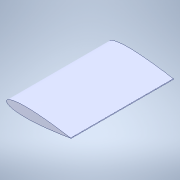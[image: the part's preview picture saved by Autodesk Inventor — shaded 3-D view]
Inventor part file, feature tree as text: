
AUTODESK INVENTOR PART (.ipt)
format: ipt  version: 2020 (Build 240168000, 168)  size: 158,720 bytes
history: native  units: in
note: dims shown in document units (in); Inventor stores cm internally (conversion verified against a paired STEP export)
features: other x2, direct_edit x1, plane x1, extrude x1, sketch x1, projected_geometry x1
ambient origin geometry x8: Origin, YZ Plane, XZ Plane, XY Plane, X Axis, Y Axis, Z Axis, Center Point
bodies: Solid1 (feature_tree)
feature tree (7):
  direct_edit  "Direct Edit1"
  plane  "Work Plane1"
  extrude  "Extrusion1"  [1 undecoded]
  sketch  "Sketch1"  dims[d0=0.5906in d1=0.3937in d2=0.3937in d3=-4.7244in d4=4.7244in d5=7.0866in d6=0.1575in d7=0.1575in d8=2.5in d9=2.1654in d10=0.4251in d11=0.0in]
  projected_geometry  "Projected Loop1"
  other  "Boss-Extrude1"
  other  "Scale1"
note: 1 required parameter value undecoded (feature->parameter linkage not recoverable at this tier; creation-order binding heuristic only, values carry confidence <= 0.55)
